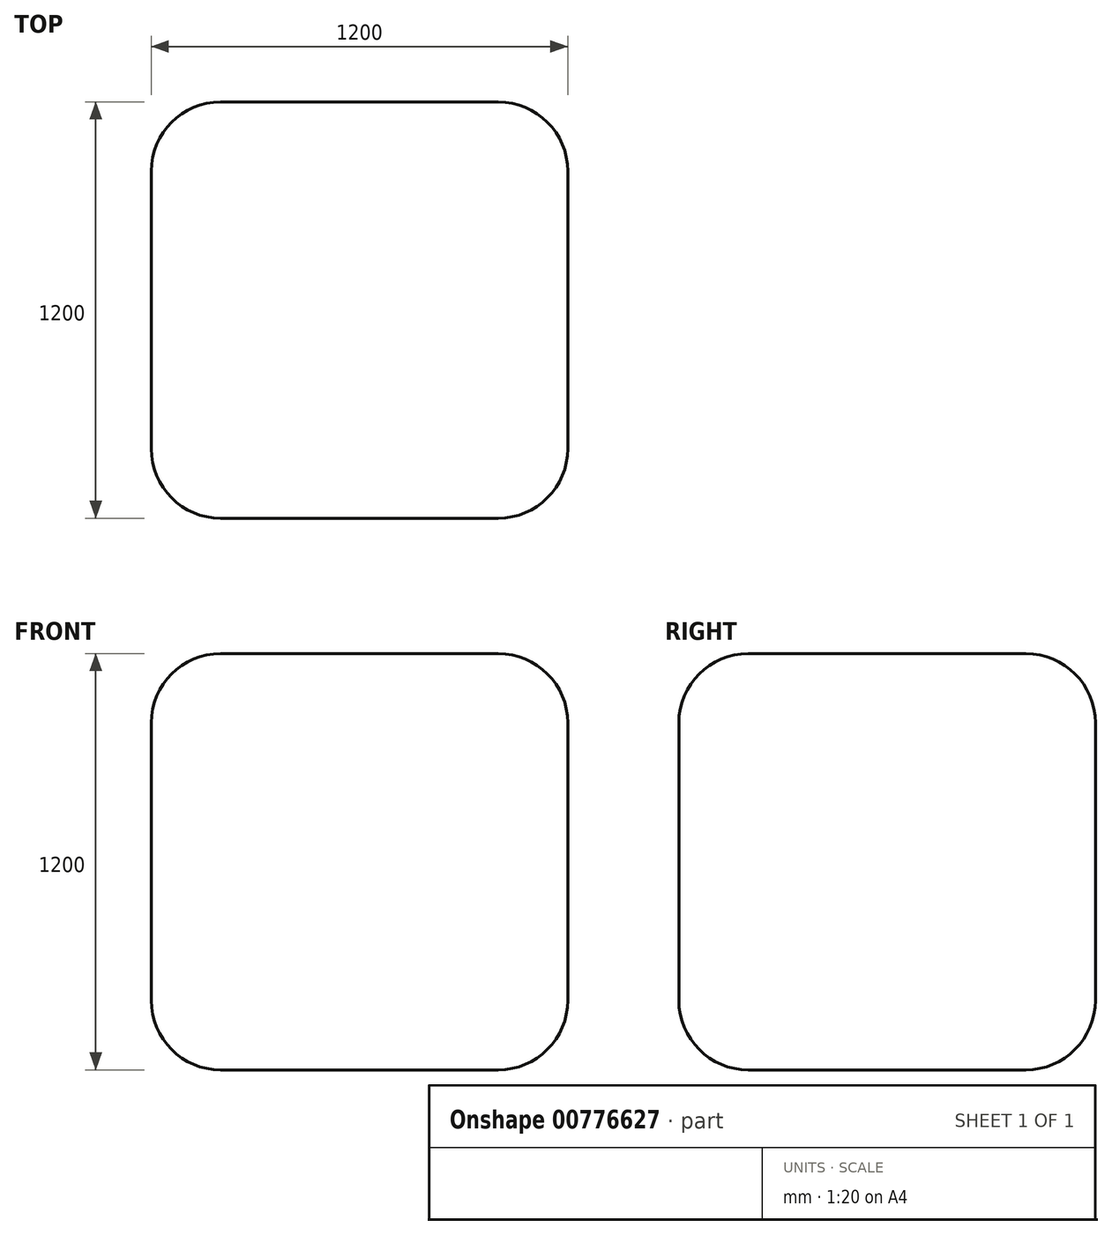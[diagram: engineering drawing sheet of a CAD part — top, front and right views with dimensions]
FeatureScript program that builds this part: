
annotation { "Feature Type Name" : "Feature", "Feature Type Description" : "" }
export const myFeature = defineFeature(function(context is Context, id is Id, definition is map)
    precondition{}
    {
        {
            var Q0;
            Q0=qCreatedBy(makeId("Top.planeOp"),FACE);
            var sketch = newSketch(context, id + "F0", { "sketchPlane" : qUnion([Q0])});
            skLineSegment(sketch, "E0.bottom", {"start": v(-600, 600) * mm, "end": v(600, 600) * mm});
            skLineSegment(sketch, "E0.top", {"start": v(-600, -600) * mm, "end": v(600, -600) * mm});
            skLineSegment(sketch, "E0.left", {"start": v(-600, 600) * mm, "end": v(-600, -600) * mm});
            skLineSegment(sketch, "E0.right", {"start": v(600, 600) * mm, "end": v(600, -600) * mm});
            skPoint(sketch, "E0.middle", {"position": v(0, 0) * mm});
            skSolve(sketch);
        }
        {
            var Q0;
            Q0 = qSketchRegion(id + "F0", true);
            extrude(context, id + "F1", {"entities" : qUnion([Q0]), "depth" : 1200 * mm, "offsetDistance" : 25 * mm});
        }
        {
            var Q0;
            Q0=makeQuery(id+"F1.opExtrude","CAP_FACE",FACE,{"disambiguationData":[OSD([sQuery(id+"F0.wireOp",EDGE,"E0.bottom"),sQuery(id+"F0.wireOp",EDGE,"E0.top"),sQuery(id+"F0.wireOp",EDGE,"E0.left"),sQuery(id+"F0.wireOp",EDGE,"E0.right")])],"isStart":false});
            var Q1;
            Q1=makeQuery(id+"F1.opExtrude","CAP_FACE",FACE,{"disambiguationData":[OSD([sQuery(id+"F0.wireOp",EDGE,"E0.bottom"),sQuery(id+"F0.wireOp",EDGE,"E0.top"),sQuery(id+"F0.wireOp",EDGE,"E0.left"),sQuery(id+"F0.wireOp",EDGE,"E0.right")])],"isStart":true});
            var Q2;
            Q2=makeQuery(id+"F1.opExtrude","SWEPT_FACE",FACE,{"disambiguationData":[OSD([sQuery(id+"F0.wireOp",EDGE,"E0.top")])]});
            var Q3;
            Q3=makeQuery(id+"F1.opExtrude","SWEPT_FACE",FACE,{"disambiguationData":[OSD([sQuery(id+"F0.wireOp",EDGE,"E0.bottom")])]});
            fillet(context, id + "F2", {"entities" : qUnion([Q0, Q1, Q2, Q3]), "radius" : 200 * mm, "tangentPropagation" : true, "allowEdgeOverflow" : false});
        }
    });
